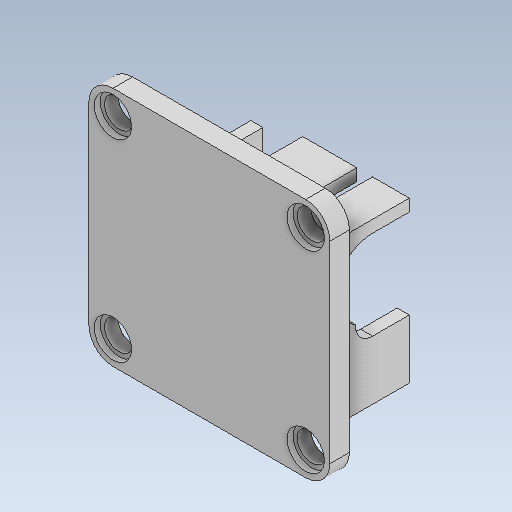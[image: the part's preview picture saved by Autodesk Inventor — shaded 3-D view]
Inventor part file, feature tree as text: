
AUTODESK INVENTOR PART (.ipt)
format: ipt  version: 2020 (Build 240168000, 168)  size: 180,224 bytes
history: native  units: mm
features: other x4, sketch x4
ambient origin geometry x8: Origin, YZ Plane, XZ Plane, XY Plane, X Axis, Y Axis, Z Axis, Center Point
bodies: Body1 (feature_tree)
feature tree (8):
  other  "apoio servo.ipt"
  other  "Sólido1::apoio servo.ipt"
  other  "OperaçãoIdentificador1"
  sketch  "Esboço1"  dims[d0=10.0mm]
  sketch  "Esboço2"
  sketch  "Esboço3"
  sketch  "Esboço4"
  other  "Sólido1"
